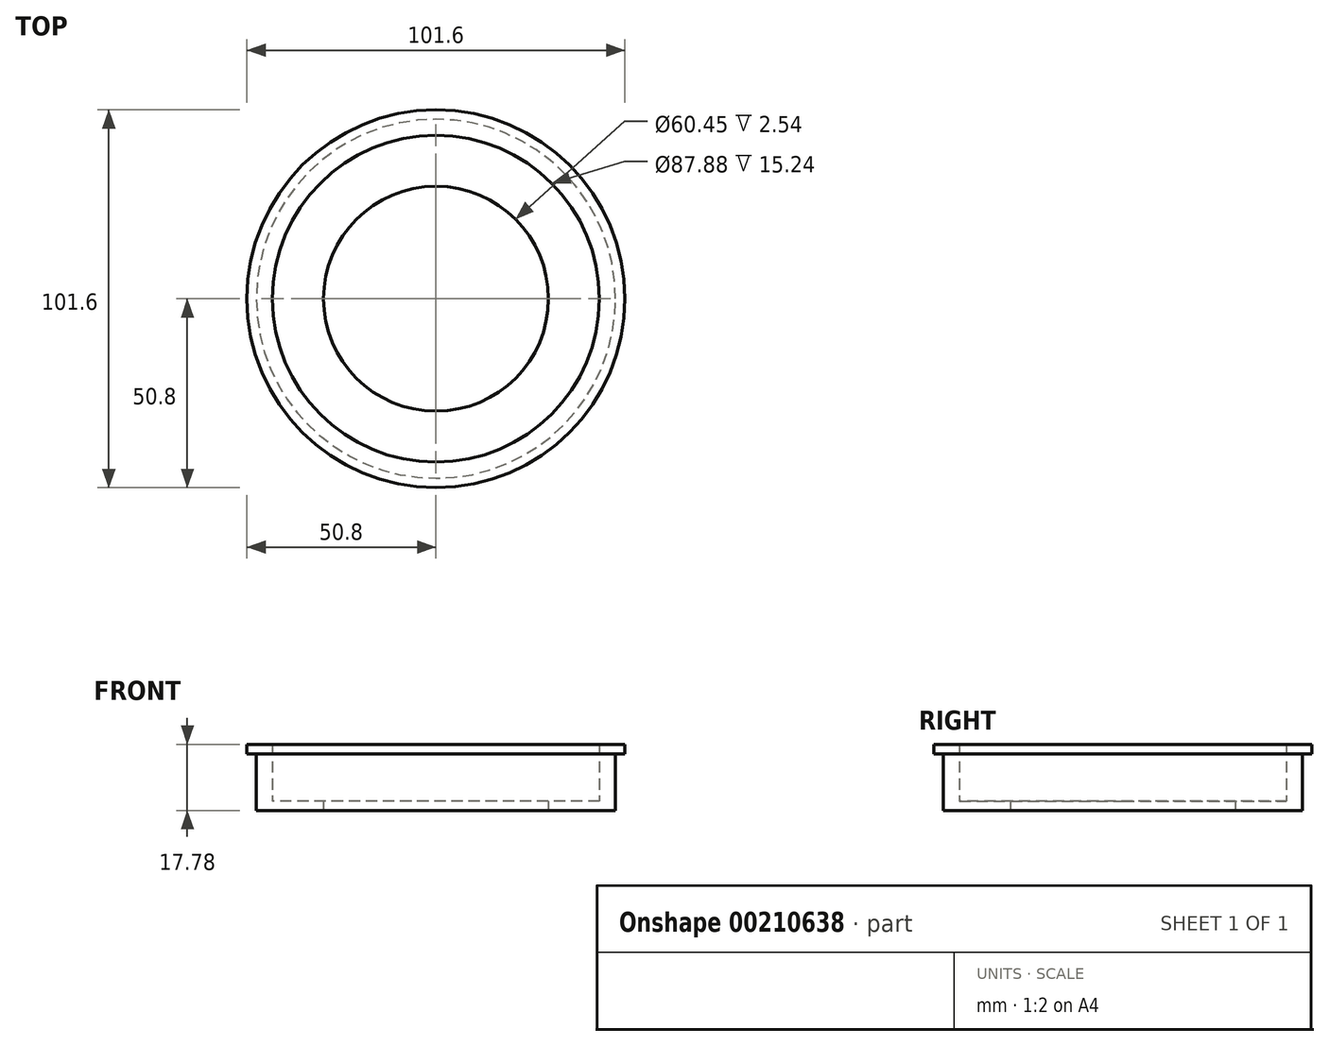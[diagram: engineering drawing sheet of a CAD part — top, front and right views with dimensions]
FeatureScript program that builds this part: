
annotation { "Feature Type Name" : "Feature", "Feature Type Description" : "" }
export const myFeature = defineFeature(function(context is Context, id is Id, definition is map)
    precondition{}
    {
        {
            var Q0;
            Q0=qCreatedBy(makeId("Top.planeOp"),FACE);
            var sketch = newSketch(context, id + "F0", { "sketchPlane" : qUnion([Q0])});
            skCircle(sketch, "E0", {"center": v(0, 0) * mm, "radius": 30.23 * mm});
            skCircle(sketch, "E1", {"center": v(0, 0) * mm, "radius": 50.8 * mm});
            skSolve(sketch);
        }
        {
            var Q0;
            Q0=makeQuery(id+"F0.imprint","IMPRINT",FACE,{"disambiguationData":[TD([[makeQuery(id+"F0.imprint","IMPRINT",EDGE,{"derivedFrom":sQuery(id+"F0.wireOp",EDGE,"E0")}),-1.0]])]});
            extrude(context, id + "F1", {"entities" : qUnion([Q0]), "depth" : 2.54 * mm});
        }
        {
            var Q0;
            Q0=makeQuery(id+"F1.opExtrude","CAP_FACE",FACE,{"disambiguationData":[OSD([sQuery(id+"F0.wireOp",EDGE,"E0"),sQuery(id+"F0.wireOp",EDGE,"E1")])],"isStart":false});
            var sketch = newSketch(context, id + "F2", { "sketchPlane" : qUnion([Q0])});
            skCircle(sketch, "E2", {"center": v(0, 0) * mm, "radius": 43.94 * mm});
            skSolve(sketch);
        }
        {
            var Q0;
            Q0=makeQuery(id+"F2.imprint","IMPRINT",FACE,{"disambiguationData":[TD([[makeQuery(id+"F2.imprint","IMPRINT",EDGE,{"derivedFrom":sQuery(id+"F2.wireOp",EDGE,"E2")}),-1.0]])]});
            extrude(context, id + "F3", {"entities" : qUnion([Q0]), "operationType" : NewBodyOperationType.ADD, "depth" : 15.24 * mm});
        }
        {
            var Q0;
            Q0=makeQuery(id+"F1.opExtrude","CAP_FACE",FACE,{"disambiguationData":[OSD([sQuery(id+"F0.wireOp",EDGE,"E0"),sQuery(id+"F0.wireOp",EDGE,"E1")])],"isStart":true});
            var sketch = newSketch(context, id + "F4", { "sketchPlane" : qUnion([Q0])});
            skCircle(sketch, "E3", {"center": v(0, 0) * mm, "radius": 48.26 * mm});
            skSolve(sketch);
        }
        {
            var Q0;
            Q0=makeQuery(id+"F4.imprint","IMPRINT",FACE,{"disambiguationData":[TD([[makeQuery(id+"F4.imprint","IMPRINT",EDGE,{"derivedFrom":sQuery(id+"F4.wireOp",EDGE,"E3")}),-1.0]])]});
            extrude(context, id + "F5", {"entities" : qUnion([Q0]), "operationType" : NewBodyOperationType.REMOVE, "oppositeDirection" : true, "depth" : 15.24 * mm});
        }
    });
